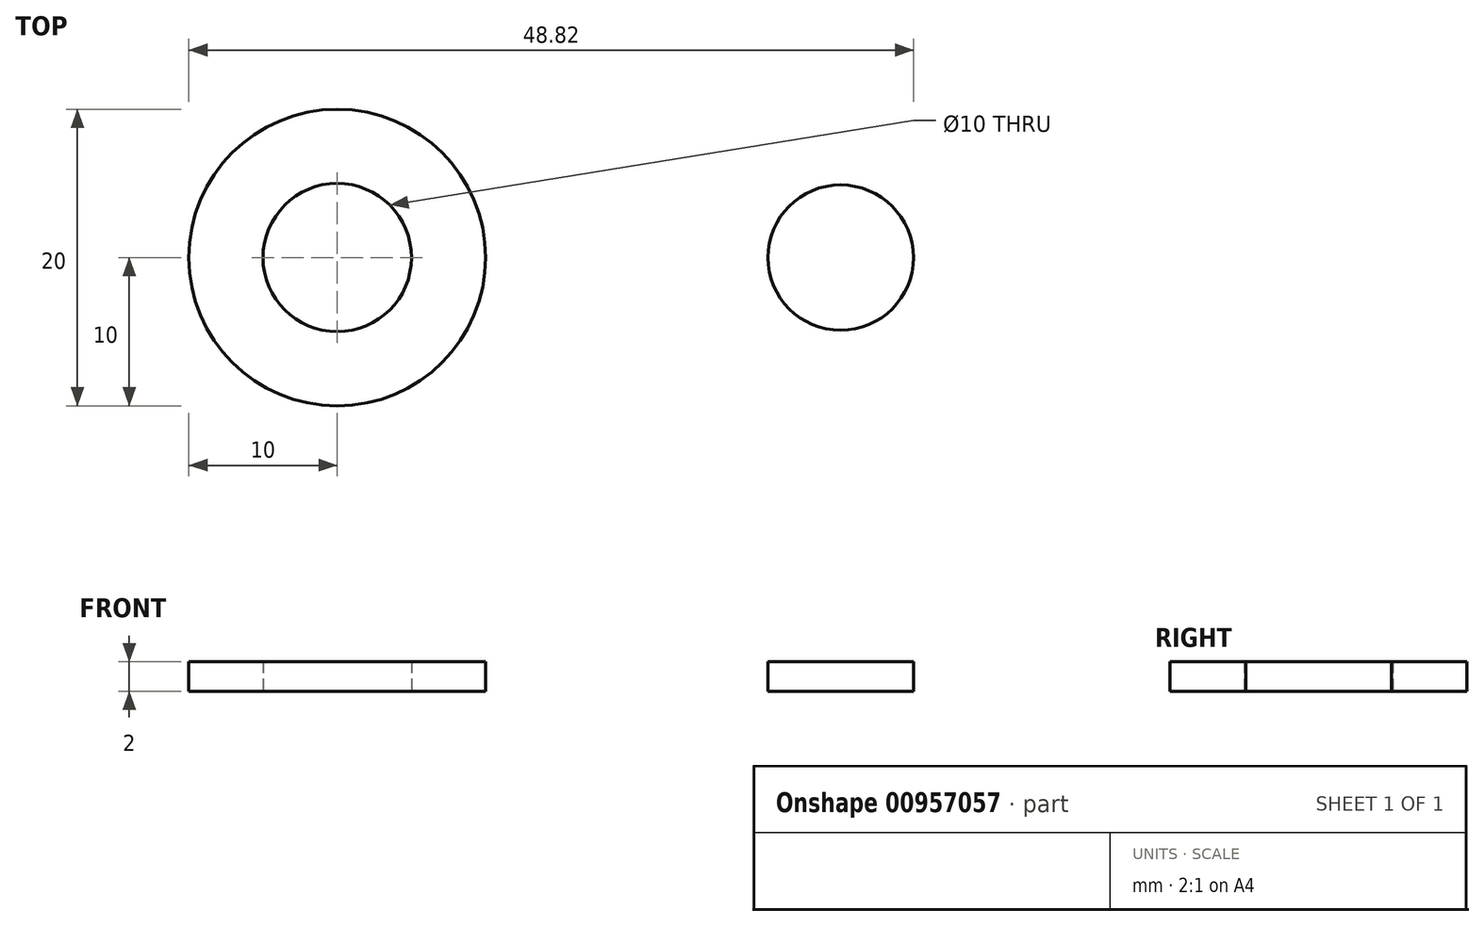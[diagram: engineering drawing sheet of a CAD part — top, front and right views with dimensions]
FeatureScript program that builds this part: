
annotation { "Feature Type Name" : "Feature", "Feature Type Description" : "" }
export const myFeature = defineFeature(function(context is Context, id is Id, definition is map)
    precondition{}
    {
        {
            var Q0;
            Q0=qCreatedBy(makeId("Top.planeOp"),FACE);
            var sketch = newSketch(context, id + "F0", { "sketchPlane" : qUnion([Q0])});
            skCircle(sketch, "E0", {"center": v(0, 0) * mm, "radius": 10 * mm});
            skCircle(sketch, "E1", {"center": v(0, 0) * mm, "radius": 5 * mm});
            skSolve(sketch);
        }
        {
            var Q0;
            Q0 = qSketchRegion(id + "F0", true);
            extrude(context, id + "F1", {"entities" : qUnion([Q0]), "depth" : 2 * mm, "offsetDistance" : 25 * mm});
        }
        {
            var Q0;
            Q0=qCreatedBy(makeId("Top.planeOp"),FACE);
            var sketch = newSketch(context, id + "F2", { "sketchPlane" : qUnion([Q0])});
            skCircle(sketch, "E2", {"center": v(33.92, 0) * mm, "radius": 4.9 * mm});
            skSolve(sketch);
        }
        {
            var Q0;
            Q0 = qSketchRegion(id + "F2", true);
            extrude(context, id + "F3", {"entities" : qUnion([Q0]), "depth" : 2 * mm, "offsetDistance" : 25 * mm});
        }
    });
